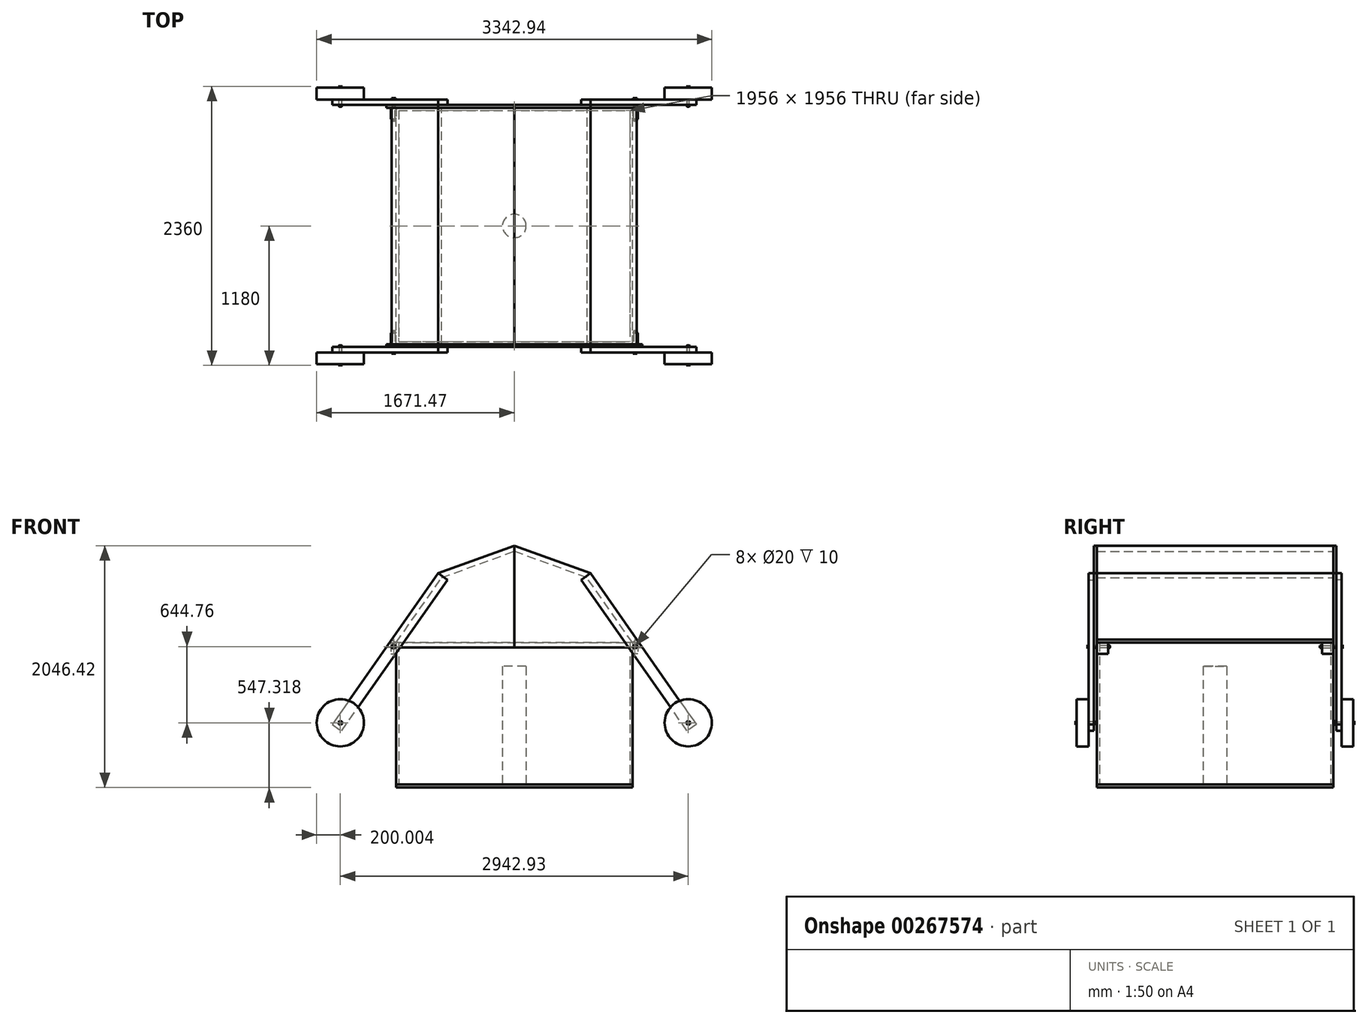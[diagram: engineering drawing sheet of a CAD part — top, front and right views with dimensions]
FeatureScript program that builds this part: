
annotation { "Feature Type Name" : "Feature", "Feature Type Description" : "" }
export const myFeature = defineFeature(function(context is Context, id is Id, definition is map)
    precondition{}
    {
        {
            var Q0;
            Q0=qCreatedBy(makeId("Top.planeOp"),FACE);
            var sketch = newSketch(context, id + "F0", { "sketchPlane" : qUnion([Q0])});
            skLineSegment(sketch, "E0.bottom", {"start": v(1000, -1000) * mm, "end": v(-1000, -1000) * mm});
            skLineSegment(sketch, "E0.top", {"start": v(1000, 1000) * mm, "end": v(-1000, 1000) * mm});
            skLineSegment(sketch, "E0.left", {"start": v(1000, -1000) * mm, "end": v(1000, 1000) * mm});
            skLineSegment(sketch, "E0.right", {"start": v(-1000, -1000) * mm, "end": v(-1000, 1000) * mm});
            skPoint(sketch, "E0.middle", {"position": v(0, 0) * mm});
            skSolve(sketch);
        }
        {
            var Q0;
            Q0 = qSketchRegion(id + "F0", true);
            extrude(context, id + "F1", {"entities" : qUnion([Q0]), "oppositeDirection" : true, "depth" : 25 * mm});
        }
        {
            var Q0;
            Q0=makeQuery(id+"F1.opExtrude","CAP_FACE",FACE,{"disambiguationData":[OSD([sQuery(id+"F0.wireOp",EDGE,"E0.bottom"),sQuery(id+"F0.wireOp",EDGE,"E0.top"),sQuery(id+"F0.wireOp",EDGE,"E0.left"),sQuery(id+"F0.wireOp",EDGE,"E0.right")])],"isStart":true});
            var sketch = newSketch(context, id + "F2", { "sketchPlane" : qUnion([Q0])});
            skLineSegment(sketch, "E1.bottom", {"start": v(-1000, 1000) * mm, "end": v(1000, 1000) * mm});
            skLineSegment(sketch, "E1.top", {"start": v(-1000, -1000) * mm, "end": v(1000, -1000) * mm});
            skLineSegment(sketch, "E1.left", {"start": v(-1000, 1000) * mm, "end": v(-1000, -1000) * mm});
            skLineSegment(sketch, "E1.right", {"start": v(1000, 1000) * mm, "end": v(1000, -1000) * mm});
            skPoint(sketch, "E1.middle", {"position": v(0, 0) * mm});
            skLineSegment(sketch, "E2.bottom", {"start": v(-978, 978) * mm, "end": v(978, 978) * mm});
            skLineSegment(sketch, "E2.top", {"start": v(-978, -978) * mm, "end": v(978, -978) * mm});
            skLineSegment(sketch, "E2.left", {"start": v(-978, 978) * mm, "end": v(-978, -978) * mm});
            skLineSegment(sketch, "E2.right", {"start": v(978, 978) * mm, "end": v(978, -978) * mm});
            skSolve(sketch);
        }
        {
            var Q0;
            Q0 = qSketchRegion(id + "F2", true);
            extrude(context, id + "F3", {"entities" : qUnion([Q0]), "depth" : 1200 * mm});
        }
        {
            var Q0;
            Q0=makeQuery(id+"F1.opExtrude","CAP_FACE",FACE,{"disambiguationData":[OSD([sQuery(id+"F0.wireOp",EDGE,"E0.bottom"),sQuery(id+"F0.wireOp",EDGE,"E0.top"),sQuery(id+"F0.wireOp",EDGE,"E0.left"),sQuery(id+"F0.wireOp",EDGE,"E0.right")])],"isStart":true});
            var sketch = newSketch(context, id + "F4", { "sketchPlane" : qUnion([Q0])});
            skCircle(sketch, "E3", {"center": v(0, 0) * mm, "radius": 100 * mm});
            skSolve(sketch);
        }
        {
            var Q0;
            Q0 = qSketchRegion(id + "F4", true);
            extrude(context, id + "F5", {"entities" : qUnion([Q0]), "depth" : 1000 * mm});
        }
        {
            var Q0;
            Q0=qCreatedBy(makeId("Front.planeOp"),FACE);
            var sketch = newSketch(context, id + "F6", { "sketchPlane" : qUnion([Q0])});
            skLineSegment(sketch, "E4", {"start": v(0, 2021.42) * mm, "end": v(-643.86, 1787.08) * mm});
            skLineSegment(sketch, "E5", {"start": v(-643.86, 1787.08) * mm, "end": v(-1036.86, 1225.81) * mm});
            skLineSegment(sketch, "E6", {"start": v(-1036.86, 1225.81) * mm, "end": v(-1000, 1200) * mm});
            skLineSegment(sketch, "E7", {"start": v(-1000, 1200) * mm, "end": v(-615.13, 1749.64) * mm});
            skLineSegment(sketch, "E8", {"start": v(-615.13, 1749.64) * mm, "end": v(0, 1973.54) * mm});
            skLineSegment(sketch, "E9", {"start": v(0, 1973.54) * mm, "end": v(0, 2021.42) * mm});
            skSolve(sketch);
        }
        {
            var Q0;
            Q0 = qSketchRegion(id + "F6", true);
            extrude(context, id + "F7", {"entities" : qUnion([Q0]), "endBound" : BoundingType.SYMMETRIC, "depth" : 2000 * mm});
        }
        {
            var Q0;
            Q0=makeQuery(id+"F7.opExtrude","CAP_FACE",FACE,{"disambiguationData":[OSD([sQuery(id+"F6.wireOp",EDGE,"E4"),sQuery(id+"F6.wireOp",EDGE,"E5"),sQuery(id+"F6.wireOp",EDGE,"E6"),sQuery(id+"F6.wireOp",EDGE,"E7"),sQuery(id+"F6.wireOp",EDGE,"E8"),sQuery(id+"F6.wireOp",EDGE,"E9")])],"isStart":false});
            var sketch = newSketch(context, id + "F8", { "sketchPlane" : qUnion([Q0])});
            skLineSegment(sketch, "E10.0", {"start": v(-643.86, 1787.08) * mm, "end": v(-1036.86, 1225.81) * mm});
            skLineSegment(sketch, "E11.0", {"start": v(0, 2021.42) * mm, "end": v(-643.86, 1787.08) * mm});
            skLineSegment(sketch, "E12", {"start": v(0, 2021.42) * mm, "end": v(0, 1160) * mm});
            skLineSegment(sketch, "E13", {"start": v(0, 1160) * mm, "end": v(-1082.94, 1160) * mm});
            skLineSegment(sketch, "E14", {"start": v(-1036.86, 1225.81) * mm, "end": v(-1082.94, 1160) * mm});
            skSolve(sketch);
        }
        {
            var Q0;
            Q0 = qSketchRegion(id + "F8", true);
            extrude(context, id + "F9", {"entities" : qUnion([Q0]), "depth" : 25 * mm});
        }
        {
            var Q0;
            Q0=makeQuery(id+"F9.opExtrude","SWEPT_BODY",BODY,{"disambiguationData":[OSD([sQuery(id+"F8.wireOp",EDGE,"E10.0"),sQuery(id+"F8.wireOp",EDGE,"E11.0"),sQuery(id+"F8.wireOp",EDGE,"E12"),sQuery(id+"F8.wireOp",EDGE,"E13"),sQuery(id+"F8.wireOp",EDGE,"fIAYJJce-11YS-9ekN-V3Wy-ALGfcL05YbhX")])]});
            var Q1;
            Q1=qCreatedBy(makeId("Front.planeOp"),FACE);
            mirror(context, id + "F10", {"entities" : qUnion([Q0]), "mirrorPlane" : qUnion([Q1])});
        }
        {
            var Q0;
            Q0=makeQuery(id+"F9.opExtrude","CAP_FACE",FACE,{"disambiguationData":[OSD([sQuery(id+"F8.wireOp",EDGE,"E10.0"),sQuery(id+"F8.wireOp",EDGE,"E11.0"),sQuery(id+"F8.wireOp",EDGE,"E12"),sQuery(id+"F8.wireOp",EDGE,"E13"),sQuery(id+"F8.wireOp",EDGE,"fIAYJJce-11YS-9ekN-V3Wy-ALGfcL05YbhX")])],"isStart":false});
            var sketch = newSketch(context, id + "F11", { "sketchPlane" : qUnion([Q0])});
            skLineSegment(sketch, "E15", {"start": v(-643.86, 1787.08) * mm, "end": v(-1539.05, 508.6) * mm});
            skLineSegment(sketch, "E16", {"start": v(-1539.05, 508.6) * mm, "end": v(-1461.24, 454.12) * mm});
            skLineSegment(sketch, "E17", {"start": v(-1461.24, 454.12) * mm, "end": v(-566.04, 1732.59) * mm});
            skLineSegment(sketch, "E18", {"start": v(-566.04, 1732.59) * mm, "end": v(-643.86, 1787.08) * mm});
            skSolve(sketch);
        }
        {
            var Q0;
            Q0 = qSketchRegion(id + "F11", true);
            extrude(context, id + "F12", {"entities" : qUnion([Q0]), "depth" : 45 * mm});
        }
        {
            var Q0;
            Q0=makeQuery(id+"F12.opExtrude","CAP_FACE",FACE,{"disambiguationData":[OSD([sQuery(id+"F11.wireOp",EDGE,"E15"),sQuery(id+"F11.wireOp",EDGE,"E16"),sQuery(id+"F11.wireOp",EDGE,"E17"),sQuery(id+"F11.wireOp",EDGE,"E18")])],"isStart":false});
            var sketch = newSketch(context, id + "F13", { "sketchPlane" : qUnion([Q0])});
            skCircle(sketch, "E19", {"center": v(-1471.47, 522.32) * mm, "radius": 200 * mm});
            skLineSegment(sketch, "E20", {"start": v(-1500.14, 481.36) * mm, "end": v(-1392.76, 634.72) * mm, "construction": true});
            skCircle(sketch, "E21", {"center": v(-1471.47, 522.32) * mm, "radius": 10 * mm});
            skSolve(sketch);
        }
        {
            var Q0;
            Q0 = qSketchRegion(id + "F13", true);
            extrude(context, id + "F14", {"entities" : qUnion([Q0]), "depth" : 100 * mm});
        }
        {
            var Q0;
            Q0=makeQuery(id+"F3.opExtrude","SWEPT_FACE",FACE,{"disambiguationData":[OSD([sQuery(id+"F2.wireOp",EDGE,"E1.left")])]});
            var sketch = newSketch(context, id + "F15", { "sketchPlane" : qUnion([Q0])});
            skLineSegment(sketch, "E22.bottom", {"start": v(1000, 1200) * mm, "end": v(905, 1200) * mm});
            skLineSegment(sketch, "E22.top", {"start": v(1000, 1105) * mm, "end": v(905, 1105) * mm});
            skLineSegment(sketch, "E22.left", {"start": v(1000, 1200) * mm, "end": v(1000, 1105) * mm});
            skLineSegment(sketch, "E22.right", {"start": v(905, 1200) * mm, "end": v(905, 1105) * mm});
            skSolve(sketch);
        }
        {
            var Q0;
            Q0 = qSketchRegion(id + "F15", true);
            extrude(context, id + "F16", {"entities" : qUnion([Q0]), "depth" : 45 * mm});
        }
        {
            var Q0;
            Q0=makeQuery(id+"F12.opExtrude","CAP_FACE",FACE,{"disambiguationData":[OSD([sQuery(id+"F11.wireOp",EDGE,"E15"),sQuery(id+"F11.wireOp",EDGE,"E16"),sQuery(id+"F11.wireOp",EDGE,"E17"),sQuery(id+"F11.wireOp",EDGE,"E18")])],"isStart":false});
            var sketch = newSketch(context, id + "F17", { "sketchPlane" : qUnion([Q0])});
            skLineSegment(sketch, "E23.0", {"start": v(-1000, 1200) * mm, "end": v(-1000, 0) * mm, "construction": true});
            skLineSegment(sketch, "E24.0", {"start": v(1000, 1200) * mm, "end": v(-1000, 1200) * mm, "construction": true});
            skCircle(sketch, "E25", {"center": v(-1020, 1167.08) * mm, "radius": 10 * mm});
            skLineSegment(sketch, "E26", {"start": v(-1091.87, 1064.43) * mm, "end": v(-951.17, 1265.38) * mm, "construction": true});
            skSolve(sketch);
        }
        {
            var Q0;
            Q0 = qSketchRegion(id + "F17", true);
            extrude(context, id + "F18", {"entities" : qUnion([Q0]), "operationType" : NewBodyOperationType.REMOVE, "endBound" : BoundingType.THROUGH_ALL, "oppositeDirection" : true, "depth" : 25 * mm});
        }
        {
            var Q0;
            Q0=makeQuery(id+"F12.opExtrude","CAP_FACE",FACE,{"disambiguationData":[OSD([sQuery(id+"F11.wireOp",EDGE,"E15"),sQuery(id+"F11.wireOp",EDGE,"E16"),sQuery(id+"F11.wireOp",EDGE,"E17"),sQuery(id+"F11.wireOp",EDGE,"E18")])],"isStart":false});
            var sketch = newSketch(context, id + "F19", { "sketchPlane" : qUnion([Q0])});
            skCircle(sketch, "E27.0", {"center": v(-1020, 1167.08) * mm, "radius": 10 * mm});
            skSolve(sketch);
        }
        {
            var Q0;
            Q0 = qSketchRegion(id + "F19", true);
            extrude(context, id + "F20", {"entities" : qUnion([Q0]), "oppositeDirection" : true, "depth" : 183 * mm});
        }
        {
            var Q0;
            Q0=makeQuery(id+"F12.opExtrude","CAP_FACE",FACE,{"disambiguationData":[OSD([sQuery(id+"F11.wireOp",EDGE,"E15"),sQuery(id+"F11.wireOp",EDGE,"E16"),sQuery(id+"F11.wireOp",EDGE,"E17"),sQuery(id+"F11.wireOp",EDGE,"E18")])],"isStart":false});
            var sketch = newSketch(context, id + "F21", { "sketchPlane" : qUnion([Q0])});
            skCircle(sketch, "E28.cCircle", {"center": v(-1020, 1167.08) * mm, "radius": 15 * mm, "construction": true});
            skLineSegment(sketch, "E28.0", {"start": v(-1002.8, 1169.13) * mm, "end": v(-1009.62, 1153.21) * mm});
            skLineSegment(sketch, "E28.1", {"start": v(-1009.62, 1153.21) * mm, "end": v(-1026.82, 1151.16) * mm});
            skLineSegment(sketch, "E28.2", {"start": v(-1026.82, 1151.16) * mm, "end": v(-1037.2, 1165.02) * mm});
            skLineSegment(sketch, "E28.3", {"start": v(-1037.2, 1165.02) * mm, "end": v(-1030.38, 1180.95) * mm});
            skLineSegment(sketch, "E28.4", {"start": v(-1030.38, 1180.95) * mm, "end": v(-1013.18, 1183) * mm});
            skLineSegment(sketch, "E28.5", {"start": v(-1013.18, 1183) * mm, "end": v(-1002.8, 1169.13) * mm});
            skPoint(sketch, "E28.0.midPoint", {"position": v(-1006.21, 1161.17) * mm});
            skSolve(sketch);
        }
        {
            var Q0;
            Q0 = qSketchRegion(id + "F21", true);
            extrude(context, id + "F22", {"entities" : qUnion([Q0]), "operationType" : NewBodyOperationType.ADD, "depth" : 10 * mm});
        }
        {
            var Q0;
            Q0=makeQuery(id+"F16.opExtrude","SWEPT_FACE",FACE,{"disambiguationData":[OSD([sQuery(id+"F15.wireOp",EDGE,"E22.right")])]});
            var sketch = newSketch(context, id + "F23", { "sketchPlane" : qUnion([Q0])});
            skCircle(sketch, "E29.0.0", {"center": v(1020, 1167.08) * mm, "radius": 10 * mm});
            skCircle(sketch, "E30.cCircle", {"center": v(1020, 1167.08) * mm, "radius": 15 * mm, "construction": true});
            skLineSegment(sketch, "E30.0", {"start": v(1037.18, 1164.86) * mm, "end": v(1026.67, 1151.1) * mm});
            skLineSegment(sketch, "E30.1", {"start": v(1026.67, 1151.1) * mm, "end": v(1009.5, 1153.3) * mm});
            skLineSegment(sketch, "E30.2", {"start": v(1009.5, 1153.3) * mm, "end": v(1002.82, 1169.3) * mm});
            skLineSegment(sketch, "E30.3", {"start": v(1002.82, 1169.3) * mm, "end": v(1013.33, 1183.06) * mm});
            skLineSegment(sketch, "E30.4", {"start": v(1013.33, 1183.06) * mm, "end": v(1030.5, 1180.85) * mm});
            skLineSegment(sketch, "E30.5", {"start": v(1030.5, 1180.85) * mm, "end": v(1037.18, 1164.86) * mm});
            skPoint(sketch, "E30.0.midPoint", {"position": v(1031.92, 1157.98) * mm});
            skSolve(sketch);
        }
        {
            var Q0;
            Q0 = qSketchRegion(id + "F23", true);
            extrude(context, id + "F24", {"entities" : qUnion([Q0]), "depth" : 10 * mm});
        }
        {
            var Q0;
            Q0=makeQuery(id+"F14.opExtrude","CAP_FACE",FACE,{"disambiguationData":[OSD([sQuery(id+"F13.wireOp",EDGE,"E19"),sQuery(id+"F13.wireOp",EDGE,"E21")])],"isStart":false});
            var sketch = newSketch(context, id + "F25", { "sketchPlane" : qUnion([Q0])});
            skCircle(sketch, "E31.0", {"center": v(-1471.47, 522.32) * mm, "radius": 10 * mm});
            skSolve(sketch);
        }
        {
            var Q0;
            Q0 = qSketchRegion(id + "F25", true);
            extrude(context, id + "F26", {"entities" : qUnion([Q0]), "oppositeDirection" : true, "depth" : 160 * mm});
        }
        {
            var Q0;
            Q0=makeQuery(id+"F14.opExtrude","CAP_FACE",FACE,{"disambiguationData":[OSD([sQuery(id+"F13.wireOp",EDGE,"E19"),sQuery(id+"F13.wireOp",EDGE,"E21")])],"isStart":false});
            var sketch = newSketch(context, id + "F27", { "sketchPlane" : qUnion([Q0])});
            skCircle(sketch, "E32.cCircle", {"center": v(-1471.47, 522.32) * mm, "radius": 15 * mm, "construction": true});
            skLineSegment(sketch, "E32.0", {"start": v(-1454.66, 518.12) * mm, "end": v(-1466.7, 505.67) * mm});
            skLineSegment(sketch, "E32.1", {"start": v(-1466.7, 505.67) * mm, "end": v(-1483.5, 509.87) * mm});
            skLineSegment(sketch, "E32.2", {"start": v(-1483.5, 509.87) * mm, "end": v(-1488.27, 526.52) * mm});
            skLineSegment(sketch, "E32.3", {"start": v(-1488.27, 526.52) * mm, "end": v(-1476.23, 538.97) * mm});
            skLineSegment(sketch, "E32.4", {"start": v(-1476.23, 538.97) * mm, "end": v(-1459.43, 534.77) * mm});
            skLineSegment(sketch, "E32.5", {"start": v(-1459.43, 534.77) * mm, "end": v(-1454.66, 518.12) * mm});
            skPoint(sketch, "E32.0.midPoint", {"position": v(-1460.68, 511.9) * mm});
            skSolve(sketch);
        }
        {
            var Q0;
            Q0 = qSketchRegion(id + "F27", true);
            extrude(context, id + "F28", {"entities" : qUnion([Q0]), "operationType" : NewBodyOperationType.ADD, "depth" : 10 * mm});
        }
        {
            var Q0;
            Q0=makeQuery(id+"F12.opExtrude","CAP_FACE",FACE,{"disambiguationData":[OSD([sQuery(id+"F11.wireOp",EDGE,"E15"),sQuery(id+"F11.wireOp",EDGE,"E16"),sQuery(id+"F11.wireOp",EDGE,"E17"),sQuery(id+"F11.wireOp",EDGE,"E18")])],"isStart":true});
            var sketch = newSketch(context, id + "F29", { "sketchPlane" : qUnion([Q0])});
            skCircle(sketch, "E33.0.0", {"center": v(1471.47, 522.32) * mm, "radius": 10 * mm});
            skCircle(sketch, "E34.cCircle", {"center": v(1471.47, 522.32) * mm, "radius": 15 * mm, "construction": true});
            skLineSegment(sketch, "E34.0", {"start": v(1488.21, 526.75) * mm, "end": v(1483.67, 510.03) * mm});
            skLineSegment(sketch, "E34.1", {"start": v(1483.67, 510.03) * mm, "end": v(1466.93, 505.6) * mm});
            skLineSegment(sketch, "E34.2", {"start": v(1466.93, 505.6) * mm, "end": v(1454.72, 517.89) * mm});
            skLineSegment(sketch, "E34.3", {"start": v(1454.72, 517.89) * mm, "end": v(1459.26, 534.6) * mm});
            skLineSegment(sketch, "E34.4", {"start": v(1459.26, 534.6) * mm, "end": v(1476, 539.03) * mm});
            skLineSegment(sketch, "E34.5", {"start": v(1476, 539.03) * mm, "end": v(1488.21, 526.75) * mm});
            skPoint(sketch, "E34.0.midPoint", {"position": v(1485.94, 518.39) * mm});
            skSolve(sketch);
        }
        {
            var Q0;
            Q0 = qSketchRegion(id + "F29", true);
            extrude(context, id + "F30", {"entities" : qUnion([Q0]), "depth" : 10 * mm});
        }
        {
            var Q0;
            Q0=makeQuery(id+"F12.opExtrude","SWEPT_BODY",BODY,{"disambiguationData":[OSD([sQuery(id+"F11.wireOp",EDGE,"E15"),sQuery(id+"F11.wireOp",EDGE,"E16"),sQuery(id+"F11.wireOp",EDGE,"E17"),sQuery(id+"F11.wireOp",EDGE,"E18")])]});
            var Q1;
            Q1=makeQuery(id+"F14.opExtrude","SWEPT_BODY",BODY,{"disambiguationData":[OSD([sQuery(id+"F13.wireOp",EDGE,"E19"),sQuery(id+"F13.wireOp",EDGE,"E21")])]});
            var Q2;
            Q2=makeQuery(id+"F26.opExtrude","SWEPT_BODY",BODY,{"disambiguationData":[OSD([sQuery(id+"F25.wireOp",EDGE,"E31.0")])]});
            var Q3;
            Q3=makeQuery(id+"F20.opExtrude","SWEPT_BODY",BODY,{"disambiguationData":[OSD([sQuery(id+"F19.wireOp",EDGE,"E27.0")])]});
            var Q4;
            Q4=makeQuery(id+"F30.opExtrude","SWEPT_BODY",BODY,{"disambiguationData":[OSD([sQuery(id+"F29.wireOp",EDGE,"E33.0.0"),sQuery(id+"F29.wireOp",EDGE,"E34.0"),sQuery(id+"F29.wireOp",EDGE,"E34.1"),sQuery(id+"F29.wireOp",EDGE,"E34.2"),sQuery(id+"F29.wireOp",EDGE,"E34.3"),sQuery(id+"F29.wireOp",EDGE,"E34.4"),sQuery(id+"F29.wireOp",EDGE,"E34.5")])]});
            var Q5;
            Q5=makeQuery(id+"F24.opExtrude","SWEPT_BODY",BODY,{"disambiguationData":[OSD([sQuery(id+"F23.wireOp",EDGE,"E29.0.0"),sQuery(id+"F23.wireOp",EDGE,"E30.0"),sQuery(id+"F23.wireOp",EDGE,"E30.1"),sQuery(id+"F23.wireOp",EDGE,"E30.2"),sQuery(id+"F23.wireOp",EDGE,"E30.3"),sQuery(id+"F23.wireOp",EDGE,"E30.4"),sQuery(id+"F23.wireOp",EDGE,"E30.5")])]});
            var Q6;
            Q6=makeQuery(id+"F16.opExtrude","SWEPT_BODY",BODY,{"disambiguationData":[OSD([sQuery(id+"F15.wireOp",EDGE,"E22.bottom"),sQuery(id+"F15.wireOp",EDGE,"E22.top"),sQuery(id+"F15.wireOp",EDGE,"E22.left"),sQuery(id+"F15.wireOp",EDGE,"E22.right")])]});
            var Q7;
            Q7=qCreatedBy(makeId("Front.planeOp"),FACE);
            mirror(context, id + "F31", {"entities" : qUnion([Q0, Q1, Q2, Q3, Q4, Q5, Q6]), "mirrorPlane" : qUnion([Q7])});
        }
        {
            var Q0;
            Q0=makeQuery(id+"F7.opExtrude","SWEPT_BODY",BODY,{"disambiguationData":[OSD([sQuery(id+"F6.wireOp",EDGE,"E4"),sQuery(id+"F6.wireOp",EDGE,"E5"),sQuery(id+"F6.wireOp",EDGE,"E6"),sQuery(id+"F6.wireOp",EDGE,"E7"),sQuery(id+"F6.wireOp",EDGE,"E8"),sQuery(id+"F6.wireOp",EDGE,"E9")])]});
            var Q1;
            Q1=makeQuery(id+"F9.opExtrude","SWEPT_BODY",BODY,{"disambiguationData":[OSD([sQuery(id+"F8.wireOp",EDGE,"E10.0"),sQuery(id+"F8.wireOp",EDGE,"E11.0"),sQuery(id+"F8.wireOp",EDGE,"E12"),sQuery(id+"F8.wireOp",EDGE,"E13"),sQuery(id+"F8.wireOp",EDGE,"E14")])]});
            var Q2;
            Q2=makeQuery(id+"F14.opExtrude","SWEPT_BODY",BODY,{"disambiguationData":[OSD([sQuery(id+"F13.wireOp",EDGE,"E19"),sQuery(id+"F13.wireOp",EDGE,"E21")])]});
            var Q3;
            Q3=makeQuery(id+"F12.opExtrude","SWEPT_BODY",BODY,{"disambiguationData":[OSD([sQuery(id+"F11.wireOp",EDGE,"E15"),sQuery(id+"F11.wireOp",EDGE,"E16"),sQuery(id+"F11.wireOp",EDGE,"E17"),sQuery(id+"F11.wireOp",EDGE,"E18")])]});
            var Q4;
            Q4=makeQuery(id+"F31.opPattern","COPY",BODY,{"derivedFrom":makeQuery(id+"F30.opExtrude","SWEPT_BODY",BODY,{"disambiguationData":[OSD([sQuery(id+"F29.wireOp",EDGE,"E33.0.0"),sQuery(id+"F29.wireOp",EDGE,"E34.0"),sQuery(id+"F29.wireOp",EDGE,"E34.1"),sQuery(id+"F29.wireOp",EDGE,"E34.2"),sQuery(id+"F29.wireOp",EDGE,"E34.3"),sQuery(id+"F29.wireOp",EDGE,"E34.4"),sQuery(id+"F29.wireOp",EDGE,"E34.5")])]}),"instanceName":"1"});
            var Q5;
            Q5=makeQuery(id+"F31.opPattern","COPY",BODY,{"derivedFrom":makeQuery(id+"F26.opExtrude","SWEPT_BODY",BODY,{"disambiguationData":[OSD([sQuery(id+"F25.wireOp",EDGE,"E31.0")])]}),"instanceName":"1"});
            var Q6;
            Q6=makeQuery(id+"F20.opExtrude","SWEPT_BODY",BODY,{"disambiguationData":[OSD([sQuery(id+"F19.wireOp",EDGE,"E27.0")])]});
            var Q7;
            Q7=makeQuery(id+"F31.opPattern","COPY",BODY,{"derivedFrom":makeQuery(id+"F12.opExtrude","SWEPT_BODY",BODY,{"disambiguationData":[OSD([sQuery(id+"F11.wireOp",EDGE,"E15"),sQuery(id+"F11.wireOp",EDGE,"E16"),sQuery(id+"F11.wireOp",EDGE,"E17"),sQuery(id+"F11.wireOp",EDGE,"E18")])]}),"instanceName":"1"});
            var Q8;
            Q8=makeQuery(id+"F31.opPattern","COPY",BODY,{"derivedFrom":makeQuery(id+"F14.opExtrude","SWEPT_BODY",BODY,{"disambiguationData":[OSD([sQuery(id+"F13.wireOp",EDGE,"E19"),sQuery(id+"F13.wireOp",EDGE,"E21")])]}),"instanceName":"1"});
            var Q9;
            Q9=makeQuery(id+"F26.opExtrude","SWEPT_BODY",BODY,{"disambiguationData":[OSD([sQuery(id+"F25.wireOp",EDGE,"E31.0")])]});
            var Q10;
            Q10=makeQuery(id+"F10.opPattern","COPY",BODY,{"derivedFrom":makeQuery(id+"F9.opExtrude","SWEPT_BODY",BODY,{"disambiguationData":[OSD([sQuery(id+"F8.wireOp",EDGE,"E10.0"),sQuery(id+"F8.wireOp",EDGE,"E11.0"),sQuery(id+"F8.wireOp",EDGE,"E12"),sQuery(id+"F8.wireOp",EDGE,"E13"),sQuery(id+"F8.wireOp",EDGE,"E14")])]}),"instanceName":"1"});
            var Q11;
            Q11=makeQuery(id+"F16.opExtrude","SWEPT_BODY",BODY,{"disambiguationData":[OSD([sQuery(id+"F15.wireOp",EDGE,"E22.bottom"),sQuery(id+"F15.wireOp",EDGE,"E22.top"),sQuery(id+"F15.wireOp",EDGE,"E22.left"),sQuery(id+"F15.wireOp",EDGE,"E22.right")])]});
            var Q12;
            Q12=makeQuery(id+"F31.opPattern","COPY",BODY,{"derivedFrom":makeQuery(id+"F24.opExtrude","SWEPT_BODY",BODY,{"disambiguationData":[OSD([sQuery(id+"F23.wireOp",EDGE,"E29.0.0"),sQuery(id+"F23.wireOp",EDGE,"E30.0"),sQuery(id+"F23.wireOp",EDGE,"E30.1"),sQuery(id+"F23.wireOp",EDGE,"E30.2"),sQuery(id+"F23.wireOp",EDGE,"E30.3"),sQuery(id+"F23.wireOp",EDGE,"E30.4"),sQuery(id+"F23.wireOp",EDGE,"E30.5")])]}),"instanceName":"1"});
            var Q13;
            Q13=makeQuery(id+"F31.opPattern","COPY",BODY,{"derivedFrom":makeQuery(id+"F20.opExtrude","SWEPT_BODY",BODY,{"disambiguationData":[OSD([sQuery(id+"F19.wireOp",EDGE,"E27.0")])]}),"instanceName":"1"});
            var Q14;
            Q14=makeQuery(id+"F30.opExtrude","SWEPT_BODY",BODY,{"disambiguationData":[OSD([sQuery(id+"F29.wireOp",EDGE,"E33.0.0"),sQuery(id+"F29.wireOp",EDGE,"E34.0"),sQuery(id+"F29.wireOp",EDGE,"E34.1"),sQuery(id+"F29.wireOp",EDGE,"E34.2"),sQuery(id+"F29.wireOp",EDGE,"E34.3"),sQuery(id+"F29.wireOp",EDGE,"E34.4"),sQuery(id+"F29.wireOp",EDGE,"E34.5")])]});
            var Q15;
            Q15=makeQuery(id+"F31.opPattern","COPY",BODY,{"derivedFrom":makeQuery(id+"F16.opExtrude","SWEPT_BODY",BODY,{"disambiguationData":[OSD([sQuery(id+"F15.wireOp",EDGE,"E22.bottom"),sQuery(id+"F15.wireOp",EDGE,"E22.top"),sQuery(id+"F15.wireOp",EDGE,"E22.left"),sQuery(id+"F15.wireOp",EDGE,"E22.right")])]}),"instanceName":"1"});
            var Q16;
            Q16=makeQuery(id+"F24.opExtrude","SWEPT_BODY",BODY,{"disambiguationData":[OSD([sQuery(id+"F23.wireOp",EDGE,"E29.0.0"),sQuery(id+"F23.wireOp",EDGE,"E30.0"),sQuery(id+"F23.wireOp",EDGE,"E30.1"),sQuery(id+"F23.wireOp",EDGE,"E30.2"),sQuery(id+"F23.wireOp",EDGE,"E30.3"),sQuery(id+"F23.wireOp",EDGE,"E30.4"),sQuery(id+"F23.wireOp",EDGE,"E30.5")])]});
            var Q17;
            Q17=qCreatedBy(makeId("Right.planeOp"),FACE);
            mirror(context, id + "F32", {"entities" : qUnion([Q0, Q1, Q2, Q3, Q4, Q5, Q6, Q7, Q8, Q9, Q10, Q11, Q12, Q13, Q14, Q15, Q16]), "mirrorPlane" : qUnion([Q17])});
        }
    });
